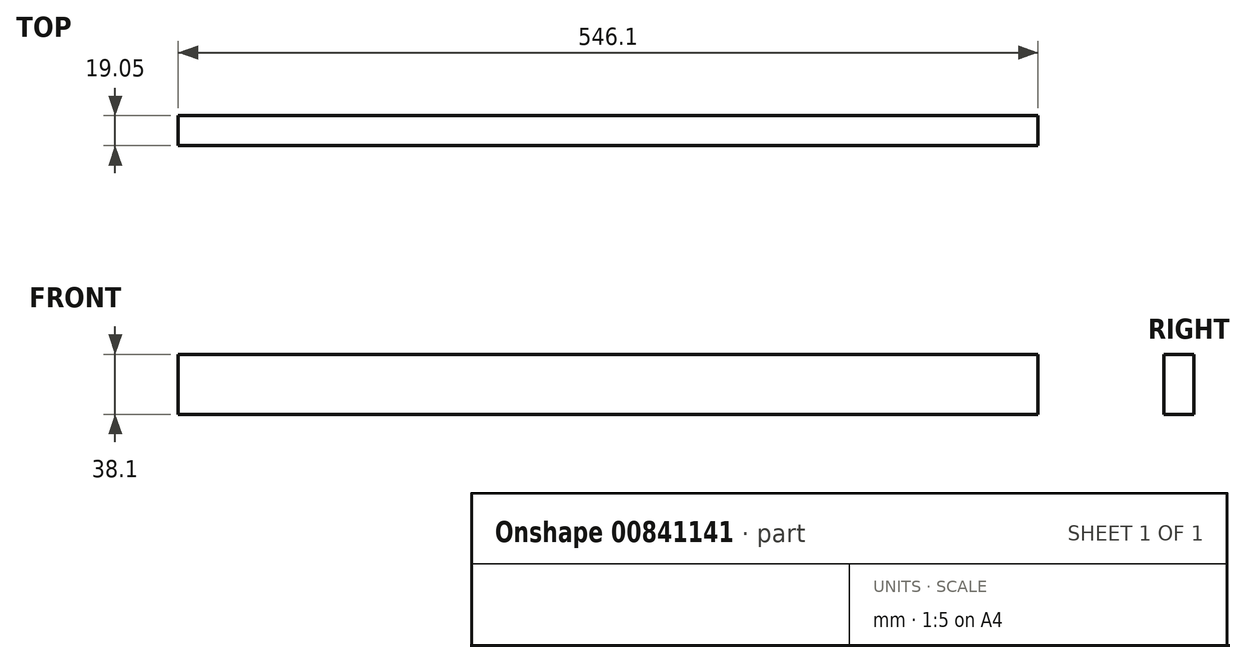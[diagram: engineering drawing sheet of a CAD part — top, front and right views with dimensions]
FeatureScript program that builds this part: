
annotation { "Feature Type Name" : "Feature", "Feature Type Description" : "" }
export const myFeature = defineFeature(function(context is Context, id is Id, definition is map)
    precondition{}
    {
        {
            var Q0;
            Q0=qCreatedBy(makeId("Front.planeOp"),FACE);
            var sketch = newSketch(context, id + "F0", { "sketchPlane" : qUnion([Q0])});
            skLineSegment(sketch, "E0.bottom", {"start": v(0, 0) * mm, "end": v(-546.1, 0) * mm});
            skLineSegment(sketch, "E0.top", {"start": v(0, 38.1) * mm, "end": v(-546.1, 38.1) * mm});
            skLineSegment(sketch, "E0.left", {"start": v(0, 0) * mm, "end": v(0, 38.1) * mm});
            skLineSegment(sketch, "E0.right", {"start": v(-546.1, 0) * mm, "end": v(-546.1, 38.1) * mm});
            skSolve(sketch);
        }
        {
            var Q0;
            Q0=makeQuery(id+"F0.imprint","IMPRINT",FACE,{"disambiguationData":[TD([[makeQuery(id+"F0.imprint","IMPRINT",EDGE,{"derivedFrom":sQuery(id+"F0.wireOp",EDGE,"E0.bottom")}),-1.0]])]});
            extrude(context, id + "F1", {"entities" : qUnion([Q0]), "depth" : 19.05 * mm, "offsetDistance" : 25.4 * mm});
        }
    });
